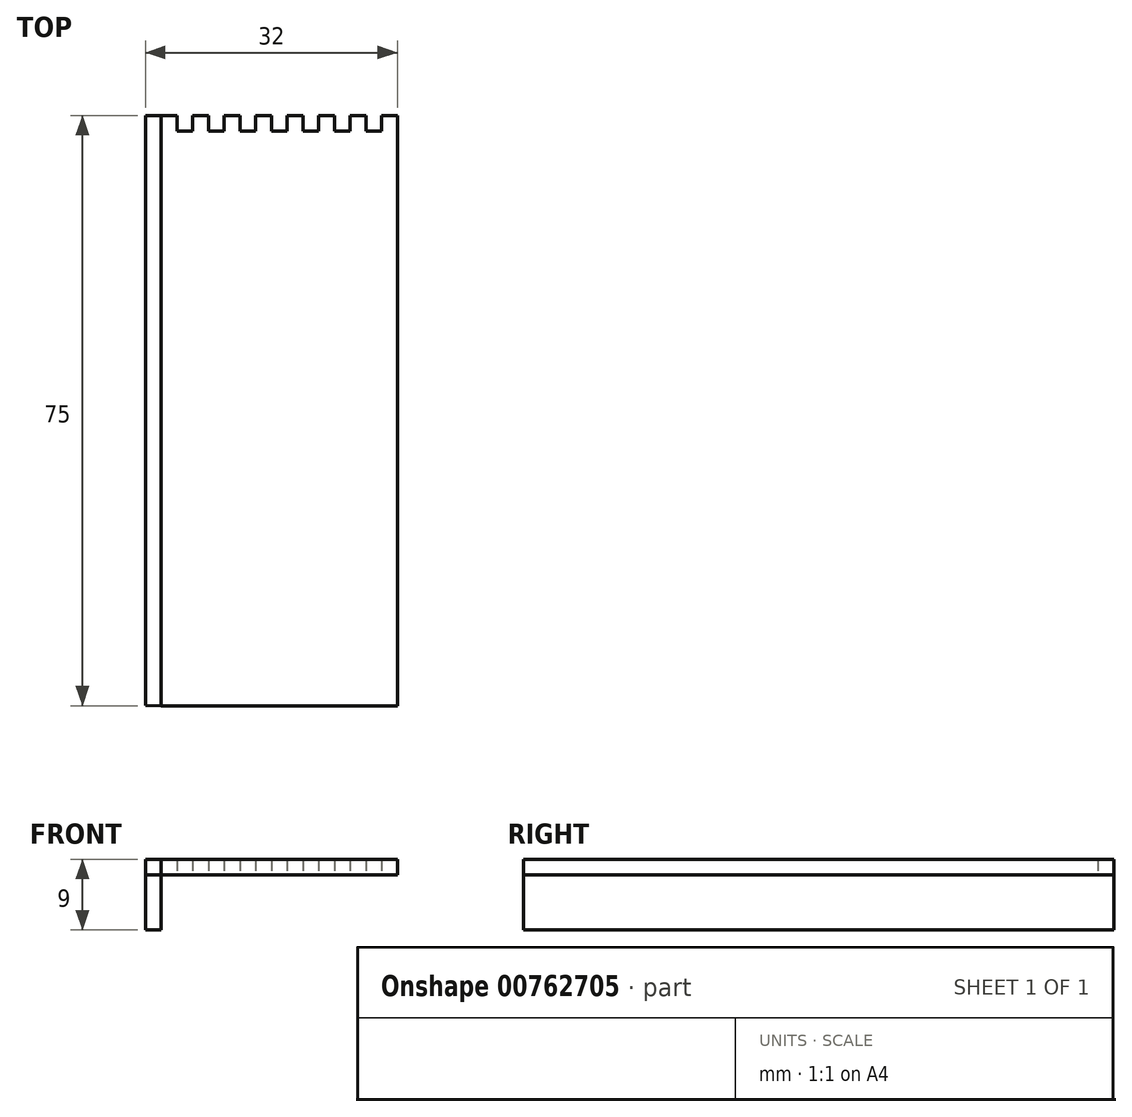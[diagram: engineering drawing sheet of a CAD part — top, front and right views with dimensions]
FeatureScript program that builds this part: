
annotation { "Feature Type Name" : "Feature", "Feature Type Description" : "" }
export const myFeature = defineFeature(function(context is Context, id is Id, definition is map)
    precondition{}
    {
        {
            var Q0;
            Q0=qCreatedBy(makeId("Top.planeOp"),FACE);
            var sketch = newSketch(context, id + "F0", { "sketchPlane" : qUnion([Q0])});
            skLineSegment(sketch, "E0.top", {"start": v(-15, -37.5) * mm, "end": v(15, -37.5) * mm});
            skLineSegment(sketch, "E0.left", {"start": v(-15, 37.5) * mm, "end": v(-15, -37.5) * mm});
            skLineSegment(sketch, "E0.right", {"start": v(15, 37.5) * mm, "end": v(15, -37.5) * mm});
            skPoint(sketch, "E0.middle", {"position": v(0, 0) * mm});
            skLineSegment(sketch, "E1", {"start": v(-15, 37.5) * mm, "end": v(-13, 37.5) * mm});
            skLineSegment(sketch, "E2", {"start": v(-13, 37.5) * mm, "end": v(-13, 35.5) * mm});
            skLineSegment(sketch, "E3", {"start": v(-13, 35.5) * mm, "end": v(-11, 35.5) * mm});
            skLineSegment(sketch, "E4", {"start": v(-11, 35.5) * mm, "end": v(-11, 37.5) * mm});
            skLineSegment(sketch, "E5", {"start": v(-11, 37.5) * mm, "end": v(-9, 37.5) * mm});
            skLineSegment(sketch, "E6", {"start": v(-9, 37.5) * mm, "end": v(-9, 35.5) * mm});
            skLineSegment(sketch, "E7", {"start": v(-9, 35.5) * mm, "end": v(-7, 35.5) * mm});
            skLineSegment(sketch, "E8", {"start": v(-7, 35.5) * mm, "end": v(-7, 37.5) * mm});
            skLineSegment(sketch, "E9", {"start": v(-7, 37.5) * mm, "end": v(-5, 37.5) * mm});
            skLineSegment(sketch, "E10", {"start": v(-5, 37.5) * mm, "end": v(-5, 35.5) * mm});
            skLineSegment(sketch, "E11", {"start": v(-5, 35.5) * mm, "end": v(-3, 35.5) * mm});
            skLineSegment(sketch, "E12", {"start": v(-3, 35.5) * mm, "end": v(-3, 37.5) * mm});
            skLineSegment(sketch, "E13", {"start": v(-3, 37.5) * mm, "end": v(-1, 37.5) * mm});
            skLineSegment(sketch, "E14", {"start": v(-1, 37.5) * mm, "end": v(-1, 35.5) * mm});
            skLineSegment(sketch, "E15", {"start": v(-1, 35.5) * mm, "end": v(1, 35.5) * mm});
            skLineSegment(sketch, "E16", {"start": v(1, 35.5) * mm, "end": v(1, 37.5) * mm});
            skLineSegment(sketch, "E17", {"start": v(1, 37.5) * mm, "end": v(3, 37.5) * mm});
            skLineSegment(sketch, "E18", {"start": v(3, 37.5) * mm, "end": v(3, 35.5) * mm});
            skLineSegment(sketch, "E19", {"start": v(3, 35.5) * mm, "end": v(5, 35.5) * mm});
            skLineSegment(sketch, "E20", {"start": v(5, 35.5) * mm, "end": v(5, 37.5) * mm});
            skPoint(sketch, "E20.endSnap0", {"position": v(-2, 37.5) * mm});
            skLineSegment(sketch, "E21", {"start": v(5, 37.5) * mm, "end": v(7, 37.5) * mm});
            skLineSegment(sketch, "E22", {"start": v(7, 37.5) * mm, "end": v(7, 35.5) * mm});
            skLineSegment(sketch, "E23", {"start": v(7, 35.5) * mm, "end": v(9, 35.5) * mm});
            skLineSegment(sketch, "E24", {"start": v(9, 35.5) * mm, "end": v(9, 37.5) * mm});
            skLineSegment(sketch, "E25", {"start": v(9, 37.5) * mm, "end": v(11, 37.5) * mm});
            skLineSegment(sketch, "E26", {"start": v(11, 37.5) * mm, "end": v(11, 35.5) * mm});
            skLineSegment(sketch, "E27", {"start": v(11, 35.5) * mm, "end": v(13, 35.5) * mm});
            skLineSegment(sketch, "E28", {"start": v(13, 35.5) * mm, "end": v(13, 37.5) * mm});
            skLineSegment(sketch, "E29", {"start": v(13, 37.5) * mm, "end": v(15, 37.5) * mm});
            skLineSegment(sketch, "E30", {"start": v(-15, 37.5) * mm, "end": v(-17, 37.5) * mm});
            skLineSegment(sketch, "E31", {"start": v(-17, 37.5) * mm, "end": v(-17, -37.45) * mm});
            skLineSegment(sketch, "E32", {"start": v(-17, -37.45) * mm, "end": v(-15, -37.5) * mm});
            skSolve(sketch);
        }
        {
            var Q0;
            Q0=makeQuery(id+"F0.imprint","IMPRINT",FACE,{"disambiguationData":[TD([[makeQuery(id+"F0.imprint","IMPRINT",EDGE,{"derivedFrom":sQuery(id+"F0.wireOp",EDGE,"E0.top")}),1.0]])]});
            extrude(context, id + "F1", {"entities" : qUnion([Q0]), "depth" : 2 * mm, "offsetDistance" : 25 * mm});
        }
        {
            var Q0;
            Q0=makeQuery(id+"F0.imprint","IMPRINT",FACE,{"disambiguationData":[TD([[makeQuery(id+"F0.imprint","IMPRINT",EDGE,{"derivedFrom":sQuery(id+"F0.wireOp",EDGE,"E0.left")}),-1.0]])]});
            extrude(context, id + "F2", {"entities" : qUnion([Q0]), "operationType" : NewBodyOperationType.ADD, "oppositeDirection" : true, "depth" : 7 * mm, "offsetDistance" : 25 * mm});
        }
        {
            var Q0;
            Q0=makeQuery(id+"F0.imprint","IMPRINT",FACE,{"disambiguationData":[TD([[makeQuery(id+"F0.imprint","IMPRINT",EDGE,{"derivedFrom":sQuery(id+"F0.wireOp",EDGE,"E0.left")}),-1.0]])]});
            extrude(context, id + "F3", {"entities" : qUnion([Q0]), "depth" : 2 * mm, "offsetDistance" : 25 * mm});
        }
    });
